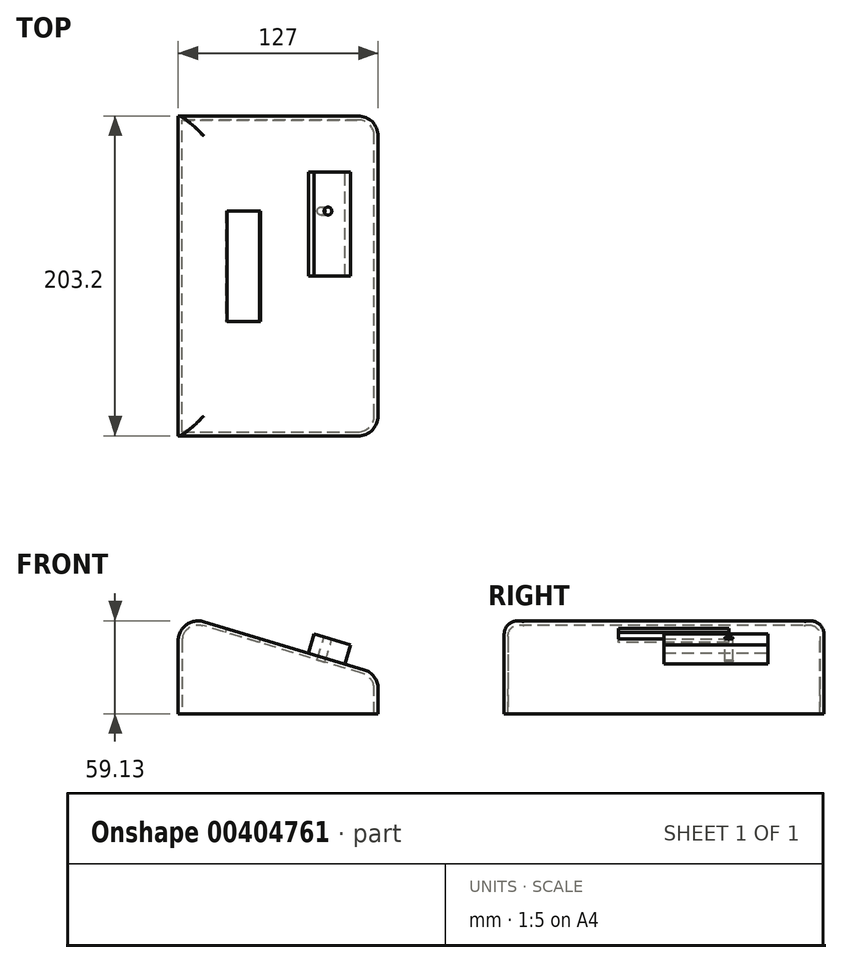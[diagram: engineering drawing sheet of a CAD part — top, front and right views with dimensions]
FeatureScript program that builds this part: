
annotation { "Feature Type Name" : "Feature", "Feature Type Description" : "" }
export const myFeature = defineFeature(function(context is Context, id is Id, definition is map)
    precondition{}
    {
        {
            var Q0;
            Q0=qCreatedBy(makeId("Front.planeOp"),FACE);
            var sketch = newSketch(context, id + "F0", { "sketchPlane" : qUnion([Q0])});
            skLineSegment(sketch, "E0", {"start": v(-1.25, 25.49) * mm, "end": v(125.75, 25.49) * mm});
            skLineSegment(sketch, "E1", {"start": v(125.75, 25.49) * mm, "end": v(125.75, 50.89) * mm});
            skLineSegment(sketch, "E2", {"start": v(125.75, 50.89) * mm, "end": v(-1.25, 88.99) * mm});
            skLineSegment(sketch, "E3", {"start": v(-1.25, 88.99) * mm, "end": v(-1.25, 25.49) * mm});
            skSolve(sketch);
        }
        {
            var Q0;
            Q0=makeQuery(id+"F0.imprint","IMPRINT",FACE,{"disambiguationData":[TD([[makeQuery(id+"F0.imprint","IMPRINT",EDGE,{"derivedFrom":sQuery(id+"F0.wireOp",EDGE,"E0")}),1.0]])]});
            extrude(context, id + "F1", {"entities" : qUnion([Q0]), "depth" : 203.2 * mm});
        }
        {
            var Q0;
            Q0=makeQuery(id+"F1.opExtrude","SWEPT_EDGE",EDGE,{"disambiguationData":[OSD([sQuery(id+"F0.wireOp",EDGE,"E2"),sQuery(id+"F0.wireOp",EDGE,"E3")])]});
            var Q1;
            Q1=makeQuery(id+"F1.opExtrude","CAP_EDGE",EDGE,{"disambiguationData":[OSD([sQuery(id+"F0.wireOp",EDGE,"E2")])],"isStart":true});
            var Q2;
            Q2=makeQuery(id+"F1.opExtrude","SWEPT_EDGE",EDGE,{"disambiguationData":[OSD([sQuery(id+"F0.wireOp",EDGE,"E1"),sQuery(id+"F0.wireOp",EDGE,"E2")])]});
            var Q3;
            Q3=makeQuery(id+"F1.opExtrude","CAP_EDGE",EDGE,{"disambiguationData":[OSD([sQuery(id+"F0.wireOp",EDGE,"E2")])],"isStart":false});
            var Q4;
            Q4=makeQuery(id+"F1.opExtrude","CAP_EDGE",EDGE,{"disambiguationData":[OSD([sQuery(id+"F0.wireOp",EDGE,"E1")])],"isStart":false});
            var Q5;
            Q5=makeQuery(id+"F1.opExtrude","CAP_EDGE",EDGE,{"disambiguationData":[OSD([sQuery(id+"F0.wireOp",EDGE,"E1")])],"isStart":true});
            fillet(context, id + "F2", {"entities" : qUnion([Q0, Q1, Q2, Q3, Q4, Q5]), "radius" : 12.7 * mm, "tangentPropagation" : true, "allowEdgeOverflow" : false});
        }
        {
            var Q0;
            Q0=makeQuery(id+"F1.opExtrude","SWEPT_FACE",FACE,{"disambiguationData":[OSD([sQuery(id+"F0.wireOp",EDGE,"E0")])]});
            shell(context, id + "F3", {"entities" : qUnion([Q0]), "thickness" : 2.54 * mm});
        }
        {
            var Q0;
            Q0=makeQuery(id+"F1.opExtrude","SWEPT_FACE",FACE,{"disambiguationData":[OSD([sQuery(id+"F0.wireOp",EDGE,"E2")])]});
            var sketch = newSketch(context, id + "F4", { "sketchPlane" : qUnion([Q0])});
            skLineSegment(sketch, "E4.bottom", {"start": v(5.5, -130.7) * mm, "end": v(27.9, -130.7) * mm});
            skLineSegment(sketch, "E4.top", {"start": v(5.5, -60.52) * mm, "end": v(27.9, -60.52) * mm});
            skLineSegment(sketch, "E4.left", {"start": v(5.5, -130.7) * mm, "end": v(5.5, -60.52) * mm});
            skLineSegment(sketch, "E4.right", {"start": v(27.9, -130.7) * mm, "end": v(27.9, -60.52) * mm});
            skSolve(sketch);
        }
        {
            var Q0;
            Q0=makeQuery(id+"F4.imprint","IMPRINT",FACE,{"disambiguationData":[TD([[makeQuery(id+"F4.imprint","IMPRINT",EDGE,{"derivedFrom":sQuery(id+"F4.wireOp",EDGE,"E4.bottom")}),1.0]])]});
            extrude(context, id + "F5", {"entities" : qUnion([Q0]), "operationType" : NewBodyOperationType.REMOVE, "oppositeDirection" : true, "depth" : 25.4 * mm});
        }
        {
            var Q0;
            Q0=makeQuery(id+"F1.opExtrude","SWEPT_FACE",FACE,{"disambiguationData":[OSD([sQuery(id+"F0.wireOp",EDGE,"E2")])]});
            var sketch = newSketch(context, id + "F6", { "sketchPlane" : qUnion([Q0])});
            skPoint(sketch, "E5.firstSnap0", {"position": v(-9.7, -101.6) * mm});
            skLineSegment(sketch, "E5.bottom", {"start": v(59.63, -101.6) * mm, "end": v(83.73, -101.6) * mm});
            skLineSegment(sketch, "E5.top", {"start": v(59.63, -35.64) * mm, "end": v(83.73, -35.64) * mm});
            skLineSegment(sketch, "E5.left", {"start": v(59.63, -101.6) * mm, "end": v(59.63, -35.64) * mm});
            skLineSegment(sketch, "E5.right", {"start": v(83.73, -101.6) * mm, "end": v(83.73, -35.64) * mm});
            skSolve(sketch);
        }
        {
            var Q0;
            Q0=makeQuery(id+"F6.imprint","IMPRINT",FACE,{"disambiguationData":[TD([[makeQuery(id+"F6.imprint","IMPRINT",EDGE,{"derivedFrom":sQuery(id+"F6.wireOp",EDGE,"E5.bottom")}),1.0]])]});
            extrude(context, id + "F7", {"entities" : qUnion([Q0]), "operationType" : NewBodyOperationType.ADD, "depth" : 12.7 * mm});
        }
        {
            var Q0;
            Q0=makeQuery(id+"F7.opExtrude","CAP_FACE",FACE,{"disambiguationData":[OSD([sQuery(id+"F6.wireOp",EDGE,"E5.bottom"),sQuery(id+"F6.wireOp",EDGE,"E5.top"),sQuery(id+"F6.wireOp",EDGE,"E5.left"),sQuery(id+"F6.wireOp",EDGE,"E5.right")])],"isStart":false});
            var sketch = newSketch(context, id + "F8", { "sketchPlane" : qUnion([Q0])});
            skPoint(sketch, "E6", {"position": v(68.74, -60.42) * mm});
            skPoint(sketch, "E7", {"position": v(68.74, -77.93) * mm});
            skSolve(sketch);
        }
        {
            var Q0;
            Q0=sQuery(id+"F8.wireOp",VERTEX,"E6");
            var Q1;
            Q1=makeQuery(id+"F1.opExtrude","SWEPT_BODY",BODY,{"disambiguationData":[OSD([sQuery(id+"F0.wireOp",EDGE,"E0"),sQuery(id+"F0.wireOp",EDGE,"E1"),sQuery(id+"F0.wireOp",EDGE,"E2"),sQuery(id+"F0.wireOp",EDGE,"E3")])]});
            hole(context, id + "F9", {"style" : HoleStyle.SIMPLE, "endStyle" : HoleEndStyle.THROUGH, "standardTappedOrClearance" : lookupTablePath({ "standard" : "ANSI", "engagement" : "75%", "pitch" : "20 tpi", "size" : "1/4", "type" : "Tapped" }), "standardBlindInLast" : lookupTablePath({ "standard" : "ANSI", "engagement" : "75%", "pitch" : "20 tpi", "size" : "1/4", "type" : "Tapped" }), "holeDiameter" : 5.1 * mm, "showTappedDepth" : true, "isTappedThrough" : true, "tappedDepth" : 12.7 * mm, "tapClearance" : 3, "locations" : qUnion([Q0]), "scope" : qUnion([Q1]), "majorDiameter" : 6.35 * mm});
        }
    });
